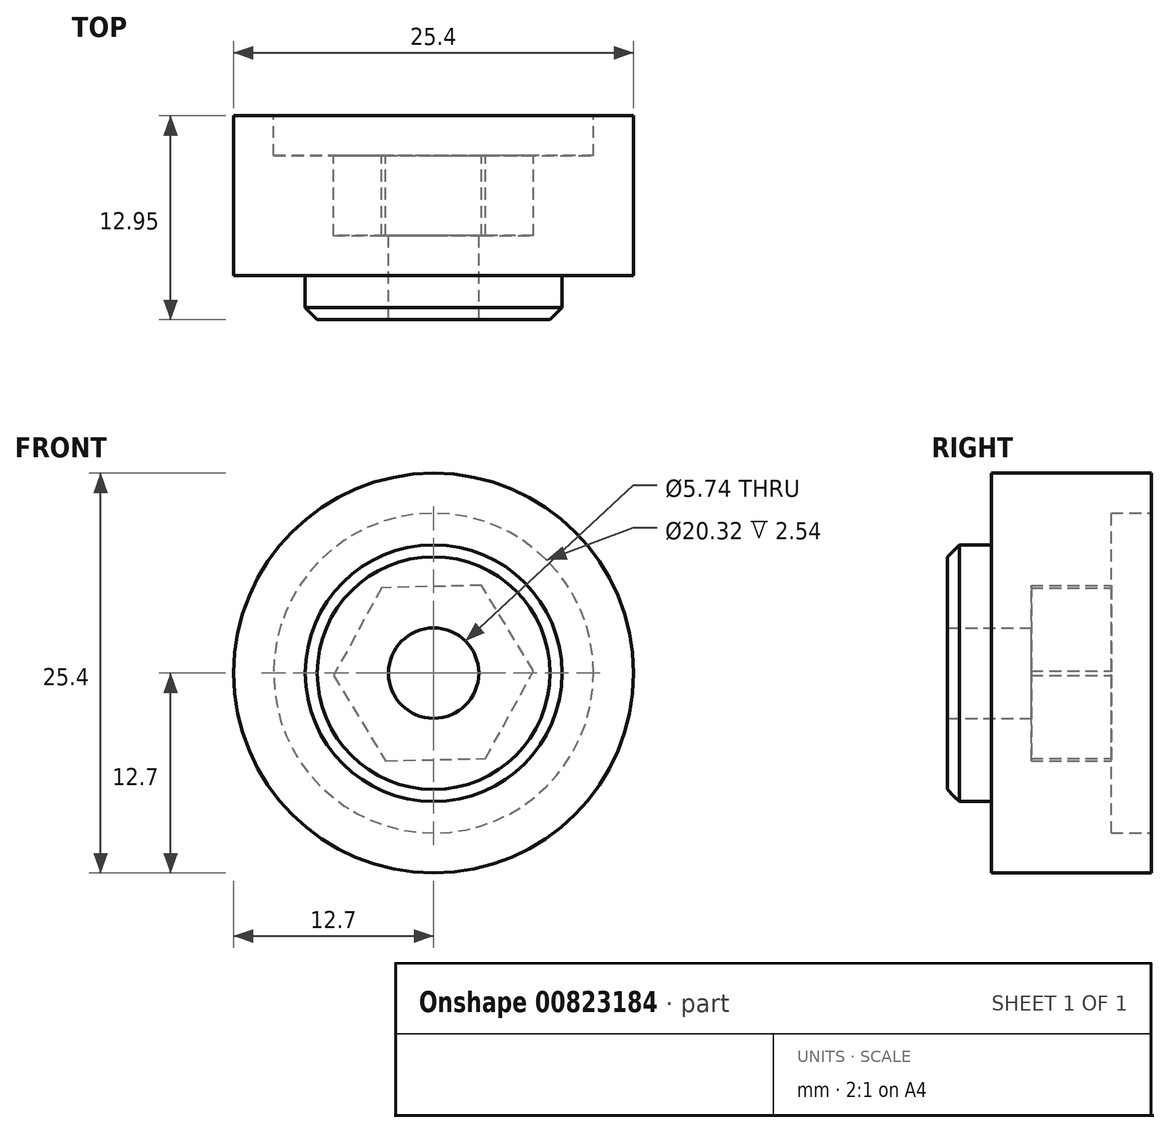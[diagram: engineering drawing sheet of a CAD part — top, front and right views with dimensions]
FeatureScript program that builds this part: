
annotation { "Feature Type Name" : "Feature", "Feature Type Description" : "" }
export const myFeature = defineFeature(function(context is Context, id is Id, definition is map)
    precondition{}
    {
        {
            var Q0;
            Q0=qCreatedBy(makeId("Front.planeOp"),FACE);
            var sketch = newSketch(context, id + "F0", { "sketchPlane" : qUnion([Q0])});
            skCircle(sketch, "E0", {"center": v(0, 0) * mm, "radius": 12.7 * mm});
            skCircle(sketch, "E1", {"center": v(0, 0) * mm, "radius": 10.16 * mm});
            skCircle(sketch, "E2", {"center": v(0, 0) * mm, "radius": 8.15 * mm});
            skCircle(sketch, "E3.cCircle", {"center": v(0, 0) * mm, "radius": 5.5 * mm, "construction": true});
            skLineSegment(sketch, "E3.0", {"start": v(3.05, 5.57) * mm, "end": v(6.35, 0.15) * mm});
            skLineSegment(sketch, "E3.1", {"start": v(6.35, 0.15) * mm, "end": v(3.3, -5.43) * mm});
            skLineSegment(sketch, "E3.2", {"start": v(3.3, -5.43) * mm, "end": v(-3.05, -5.57) * mm});
            skLineSegment(sketch, "E3.3", {"start": v(-3.05, -5.57) * mm, "end": v(-6.35, -0.15) * mm});
            skLineSegment(sketch, "E3.4", {"start": v(-6.35, -0.15) * mm, "end": v(-3.3, 5.43) * mm});
            skLineSegment(sketch, "E3.5", {"start": v(-3.3, 5.43) * mm, "end": v(3.05, 5.57) * mm});
            skPoint(sketch, "E3.0.midPoint", {"position": v(4.7, 2.86) * mm});
            skCircle(sketch, "E4", {"center": v(0, 0) * mm, "radius": 2.87 * mm});
            skSolve(sketch);
        }
        {
            var Q0;
            Q0=makeQuery(id+"F0.imprint","IMPRINT",FACE,{"disambiguationData":[TD([[makeQuery(id+"F0.imprint","IMPRINT",EDGE,{"derivedFrom":sQuery(id+"F0.wireOp",EDGE,"E0")}),1.0]])]});
            var Q1;
            Q1=makeQuery(id+"F0.imprint","IMPRINT",FACE,{"disambiguationData":[TD([[makeQuery(id+"F0.imprint","IMPRINT",EDGE,{"derivedFrom":sQuery(id+"F0.wireOp",EDGE,"E1")}),1.0]])]});
            var Q2;
            Q2=makeQuery(id+"F0.imprint","IMPRINT",FACE,{"disambiguationData":[TD([[makeQuery(id+"F0.imprint","IMPRINT",EDGE,{"derivedFrom":sQuery(id+"F0.wireOp",EDGE,"E2")}),1.0]])]});
            var Q3;
            Q3=makeQuery(id+"F0.imprint","IMPRINT",FACE,{"disambiguationData":[TD([[makeQuery(id+"F0.imprint","IMPRINT",EDGE,{"derivedFrom":sQuery(id+"F0.wireOp",EDGE,"E3.0")}),-1.0]])]});
            extrude(context, id + "F1", {"entities" : qUnion([Q0, Q1, Q2, Q3]), "depth" : 10.16 * mm, "offsetDistance" : 25.4 * mm});
        }
        {
            var Q0;
            Q0=makeQuery(id+"F0.imprint","IMPRINT",FACE,{"disambiguationData":[TD([[makeQuery(id+"F0.imprint","IMPRINT",EDGE,{"derivedFrom":sQuery(id+"F0.wireOp",EDGE,"E2")}),1.0]])]});
            var Q1;
            Q1=makeQuery(id+"F0.imprint","IMPRINT",FACE,{"disambiguationData":[TD([[makeQuery(id+"F0.imprint","IMPRINT",EDGE,{"derivedFrom":sQuery(id+"F0.wireOp",EDGE,"E3.0")}),-1.0]])]});
            extrude(context, id + "F2", {"entities" : qUnion([Q0, Q1]), "operationType" : NewBodyOperationType.ADD, "depth" : 12.95 * mm, "offsetDistance" : 25.4 * mm});
        }
        {
            var Q0;
            Q0=makeQuery(id+"F0.imprint","IMPRINT",FACE,{"disambiguationData":[TD([[makeQuery(id+"F0.imprint","IMPRINT",EDGE,{"derivedFrom":sQuery(id+"F0.wireOp",EDGE,"E1")}),1.0]])]});
            var Q1;
            Q1=makeQuery(id+"F0.imprint","IMPRINT",FACE,{"disambiguationData":[TD([[makeQuery(id+"F0.imprint","IMPRINT",EDGE,{"derivedFrom":sQuery(id+"F0.wireOp",EDGE,"E2")}),1.0]])]});
            var Q2;
            Q2=makeQuery(id+"F0.imprint","IMPRINT",FACE,{"disambiguationData":[TD([[makeQuery(id+"F0.imprint","IMPRINT",EDGE,{"derivedFrom":sQuery(id+"F0.wireOp",EDGE,"E3.0")}),-1.0]])]});
            extrude(context, id + "F3", {"entities" : qUnion([Q0, Q1, Q2]), "operationType" : NewBodyOperationType.REMOVE, "oppositeDirection" : true, "depth" : -2.54 * mm, "offsetDistance" : 25.4 * mm});
        }
        {
            var Q0;
            Q0=makeQuery(id+"F0.imprint","IMPRINT",FACE,{"disambiguationData":[TD([[makeQuery(id+"F0.imprint","IMPRINT",EDGE,{"derivedFrom":sQuery(id+"F0.wireOp",EDGE,"E3.0")}),-1.0]])]});
            extrude(context, id + "F4", {"entities" : qUnion([Q0]), "operationType" : NewBodyOperationType.REMOVE, "oppositeDirection" : true, "depth" : -7.62 * mm, "offsetDistance" : 25.4 * mm});
        }
        {
            var Q0;
            Q0=makeQuery(id+"F2.opExtrude","CAP_EDGE",EDGE,{"disambiguationData":[OSD([sQuery(id+"F0.wireOp",EDGE,"E2")])],"isStart":false});
            chamfer(context, id + "F5", {"entities" : qUnion([Q0]), "width" : 0.76 * mm, "tangentPropagation" : true});
        }
    });
